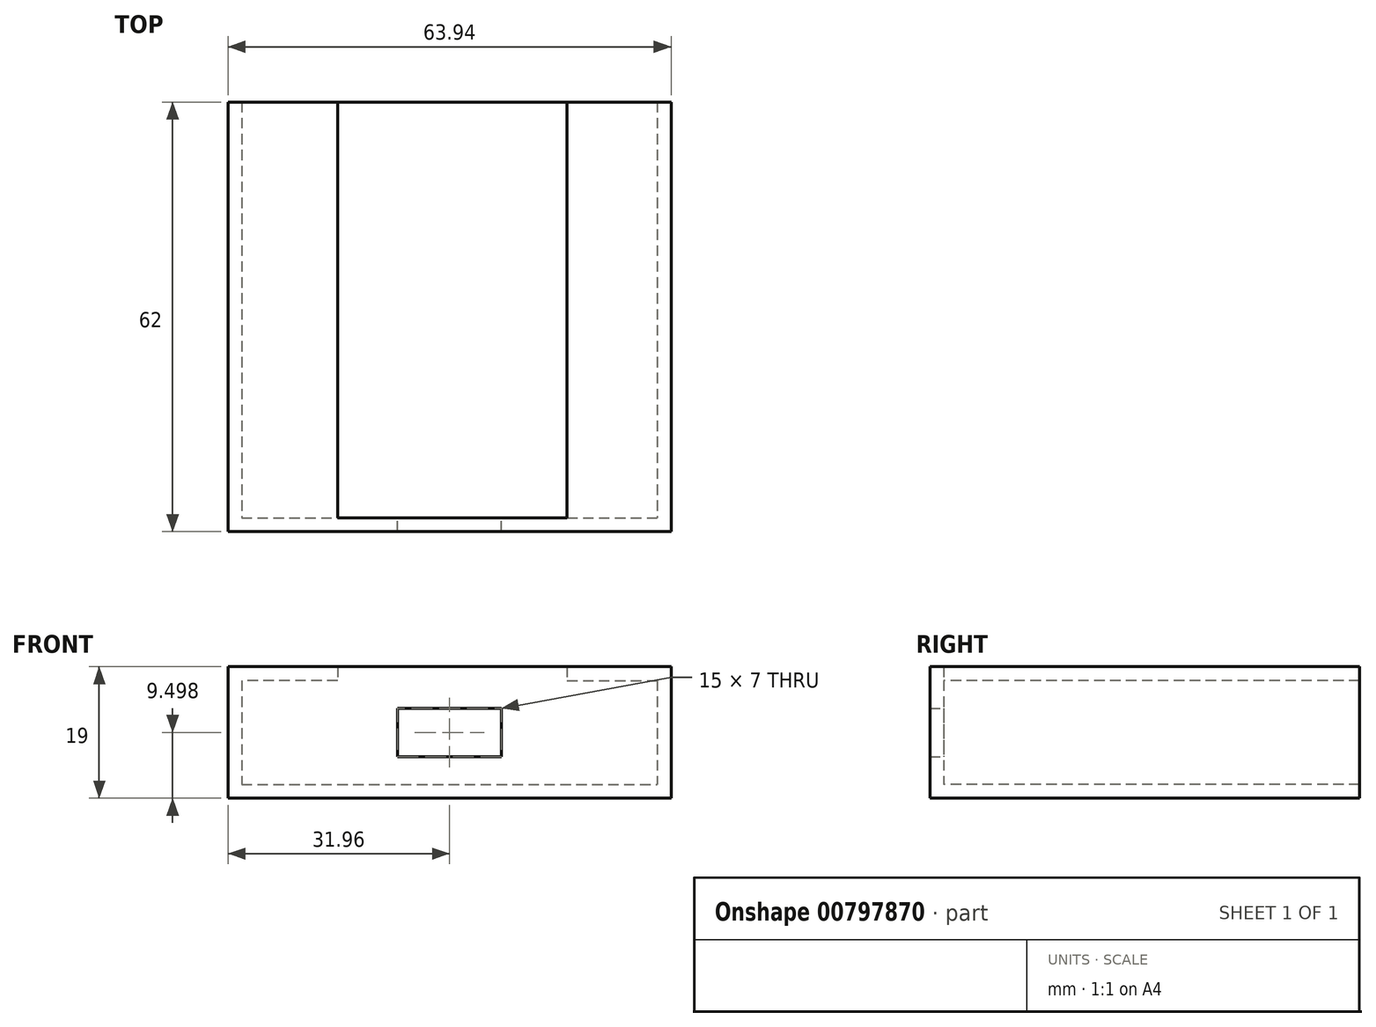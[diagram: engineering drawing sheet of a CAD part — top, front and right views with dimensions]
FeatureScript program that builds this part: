
annotation { "Feature Type Name" : "Feature", "Feature Type Description" : "" }
export const myFeature = defineFeature(function(context is Context, id is Id, definition is map)
    precondition{}
    {
        {
            var Q0;
            Q0=qCreatedBy(makeId("Front.planeOp"),FACE);
            var sketch = newSketch(context, id + "F0", { "sketchPlane" : qUnion([Q0])});
            skLineSegment(sketch, "E0", {"start": v(0, 8.64) * mm, "end": v(60, 8.64) * mm});
            skLineSegment(sketch, "E1", {"start": v(61.98, 6.64) * mm, "end": v(-2.03, 6.64) * mm});
            skLineSegment(sketch, "E2.bottom", {"start": v(37.5, 19.64) * mm, "end": v(22.5, 19.64) * mm});
            skLineSegment(sketch, "E2.top", {"start": v(37.5, 12.64) * mm, "end": v(22.5, 12.64) * mm});
            skLineSegment(sketch, "E2.left", {"start": v(37.5, 19.64) * mm, "end": v(37.5, 12.64) * mm});
            skLineSegment(sketch, "E2.right", {"start": v(22.5, 19.64) * mm, "end": v(22.5, 12.64) * mm});
            skLineSegment(sketch, "E3", {"start": v(46.98, 25.67) * mm, "end": v(46.98, 23.64) * mm});
            skLineSegment(sketch, "E4", {"start": v(46.98, 23.64) * mm, "end": v(60, 23.64) * mm});
            skLineSegment(sketch, "E5", {"start": v(-1.96, 25.64) * mm, "end": v(13.85, 25.64) * mm});
            skLineSegment(sketch, "E6", {"start": v(13.85, 25.64) * mm, "end": v(13.85, 23.64) * mm});
            skLineSegment(sketch, "E7", {"start": v(13.85, 23.64) * mm, "end": v(0, 23.64) * mm});
            skLineSegment(sketch, "E8", {"start": v(46.98, 25.67) * mm, "end": v(61.98, 25.67) * mm});
            skLineSegment(sketch, "E9", {"start": v(0, 23.64) * mm, "end": v(0, 8.64) * mm});
            skLineSegment(sketch, "E10", {"start": v(-1.96, 25.64) * mm, "end": v(-2.03, 6.64) * mm});
            skLineSegment(sketch, "E11", {"start": v(60, 23.64) * mm, "end": v(60, 8.64) * mm});
            skLineSegment(sketch, "E12", {"start": v(61.98, 25.67) * mm, "end": v(61.98, 6.64) * mm});
            skLineSegment(sketch, "E13.bottom", {"start": v(-1.96, 25.64) * mm, "end": v(61.98, 25.64) * mm});
            skLineSegment(sketch, "E13.top", {"start": v(-1.96, 6.64) * mm, "end": v(61.98, 6.64) * mm});
            skLineSegment(sketch, "E13.left", {"start": v(-1.96, 25.64) * mm, "end": v(-1.96, 6.64) * mm});
            skLineSegment(sketch, "E13.right", {"start": v(61.98, 25.64) * mm, "end": v(61.98, 6.64) * mm});
            skSolve(sketch);
        }
        {
            var Q0;
            Q0=makeQuery(id+"F0.imprint","IMPRINT",FACE,{"disambiguationData":[TD([[makeQuery(id+"F0.imprint","IMPRINT",EDGE,{"derivedFrom":sQuery(id+"F0.wireOp",EDGE,"E0")}),1.0]])]});
            var Q1;
            Q1=makeQuery(id+"F0.imprint","IMPRINT",FACE,{"disambiguationData":[TD([[makeQuery(id+"F0.imprint","IMPRINT",EDGE,{"derivedFrom":sQuery(id+"F0.wireOp",EDGE,"E0")}),-1.0]])]});
            extrude(context, id + "F1", {"entities" : qUnion([Q0, Q1]), "depth" : 2 * mm, "offsetDistance" : 25 * mm});
        }
        {
            var Q0;
            Q0=makeQuery(id+"F0.imprint","IMPRINT",FACE,{"disambiguationData":[TD([[makeQuery(id+"F0.imprint","IMPRINT",EDGE,{"derivedFrom":sQuery(id+"F0.wireOp",EDGE,"E0")}),-1.0]])]});
            extrude(context, id + "F2", {"entities" : qUnion([Q0]), "operationType" : NewBodyOperationType.ADD, "oppositeDirection" : true, "depth" : 60 * mm, "offsetDistance" : 25 * mm});
        }
    });
